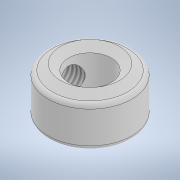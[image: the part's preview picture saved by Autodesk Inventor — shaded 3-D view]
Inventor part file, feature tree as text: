
AUTODESK INVENTOR PART (.ipt)
format: ipt  version: 2022 (Build 260153000, 153)  size: 153,088 bytes
history: native  units: mm
features: sketch x2, revolve x1, fillet x1, extrude x1, thread x1
ambient origin geometry x8: Origin, YZ Plane, XZ Plane, XY Plane, X Axis, Y Axis, Z Axis, Center Point
bodies: Solid1 (feature_tree)
feature tree (6):
  revolve  "Revolution1"  [1 undecoded]
  fillet  "Fillet1"  Radius=5.5mm
  extrude  "Extrusion1"  Depth=0.5mm
  thread  "Thread1"  [1 undecoded]
  sketch  "Sketch1"  dims[d0=2.55mm d1=5.0mm d2=5.5mm]
  sketch  "Sketch2"  dims[d4=4.8mm d5=0.5mm d6=90.0deg d7=0.5mm d8=3.0mm d9=10.0mm d10=0.0mm d11=2.938mm d12=0.0mm]
note: 2 required parameter values undecoded (feature->parameter linkage not recoverable at this tier; creation-order binding heuristic only, values carry confidence <= 0.55)